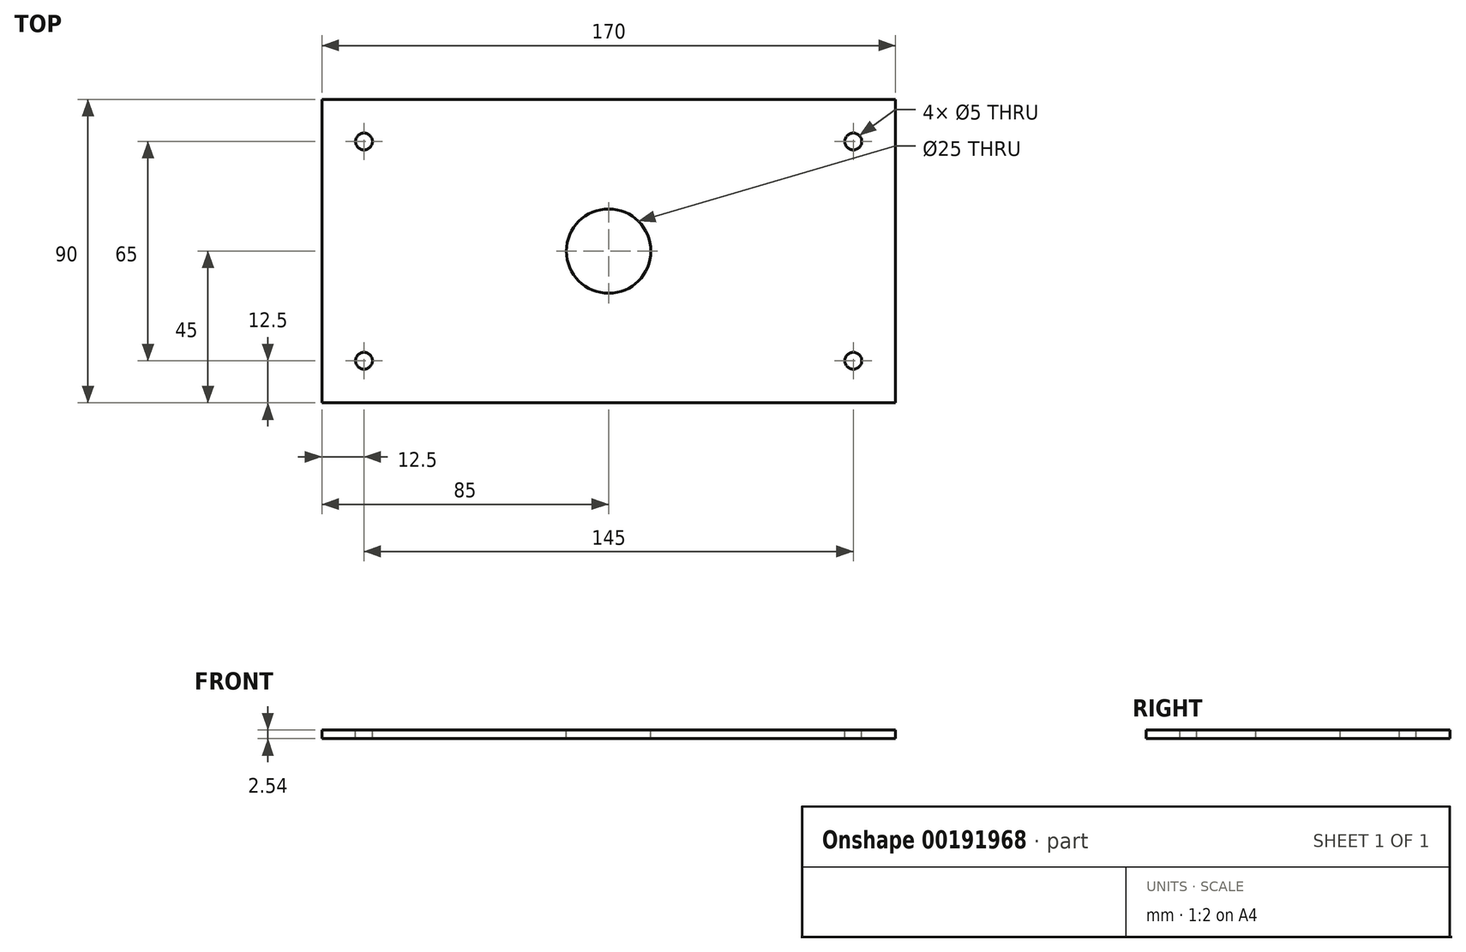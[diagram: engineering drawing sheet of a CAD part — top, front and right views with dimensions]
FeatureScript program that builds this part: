
annotation { "Feature Type Name" : "Feature", "Feature Type Description" : "" }
export const myFeature = defineFeature(function(context is Context, id is Id, definition is map)
    precondition{}
    {
        {
            var Q0;
            Q0=qCreatedBy(makeId("Top.planeOp"),FACE);
            var sketch = newSketch(context, id + "F0", { "sketchPlane" : qUnion([Q0])});
            skLineSegment(sketch, "E0.bottom", {"start": v(-85, 45) * mm, "end": v(85, 45) * mm});
            skLineSegment(sketch, "E0.top", {"start": v(-85, -45) * mm, "end": v(85, -45) * mm});
            skLineSegment(sketch, "E0.left", {"start": v(-85, 45) * mm, "end": v(-85, -45) * mm});
            skLineSegment(sketch, "E0.right", {"start": v(85, 45) * mm, "end": v(85, -45) * mm});
            skSolve(sketch);
        }
        {
            var Q0;
            Q0 = qSketchRegion(id + "F0", true);
            extrude(context, id + "F1", {"entities" : qUnion([Q0]), "depth" : 2.54 * mm});
        }
        {
            var Q0;
            Q0=makeQuery(id+"F1.opExtrude","CAP_FACE",FACE,{"disambiguationData":[OSD([sQuery(id+"F0.wireOp",EDGE,"E0.bottom"),sQuery(id+"F0.wireOp",EDGE,"E0.top"),sQuery(id+"F0.wireOp",EDGE,"E0.left"),sQuery(id+"F0.wireOp",EDGE,"E0.right")])],"isStart":false});
            var sketch = newSketch(context, id + "F2", { "sketchPlane" : qUnion([Q0])});
            skCircle(sketch, "E1", {"center": v(0, 0) * mm, "radius": 12.5 * mm});
            skSolve(sketch);
        }
        {
            var Q0;
            Q0 = qSketchRegion(id + "F2", true);
            extrude(context, id + "F3", {"entities" : qUnion([Q0]), "operationType" : NewBodyOperationType.REMOVE, "endBound" : BoundingType.THROUGH_ALL, "oppositeDirection" : true, "depth" : 25.4 * mm});
        }
        {
            var Q0;
            Q0=makeQuery(id+"F1.opExtrude","CAP_FACE",FACE,{"disambiguationData":[OSD([sQuery(id+"F0.wireOp",EDGE,"E0.bottom"),sQuery(id+"F0.wireOp",EDGE,"E0.top"),sQuery(id+"F0.wireOp",EDGE,"E0.left"),sQuery(id+"F0.wireOp",EDGE,"E0.right")])],"isStart":false});
            var sketch = newSketch(context, id + "F4", { "sketchPlane" : qUnion([Q0])});
            skCircle(sketch, "E2", {"center": v(-72.5, 32.5) * mm, "radius": 2.5 * mm});
            skCircle(sketch, "E3.MirrorC", {"center": v(72.5, 32.5) * mm, "radius": 2.5 * mm});
            skCircle(sketch, "E4.MirrorC", {"center": v(72.5, -32.5) * mm, "radius": 2.5 * mm});
            skCircle(sketch, "E5.MirrorC", {"center": v(-72.5, -32.5) * mm, "radius": 2.5 * mm});
            skSolve(sketch);
        }
        {
            var Q0;
            Q0 = qSketchRegion(id + "F4", true);
            extrude(context, id + "F5", {"entities" : qUnion([Q0]), "operationType" : NewBodyOperationType.REMOVE, "endBound" : BoundingType.THROUGH_ALL, "oppositeDirection" : true, "depth" : 25.4 * mm});
        }
    });
